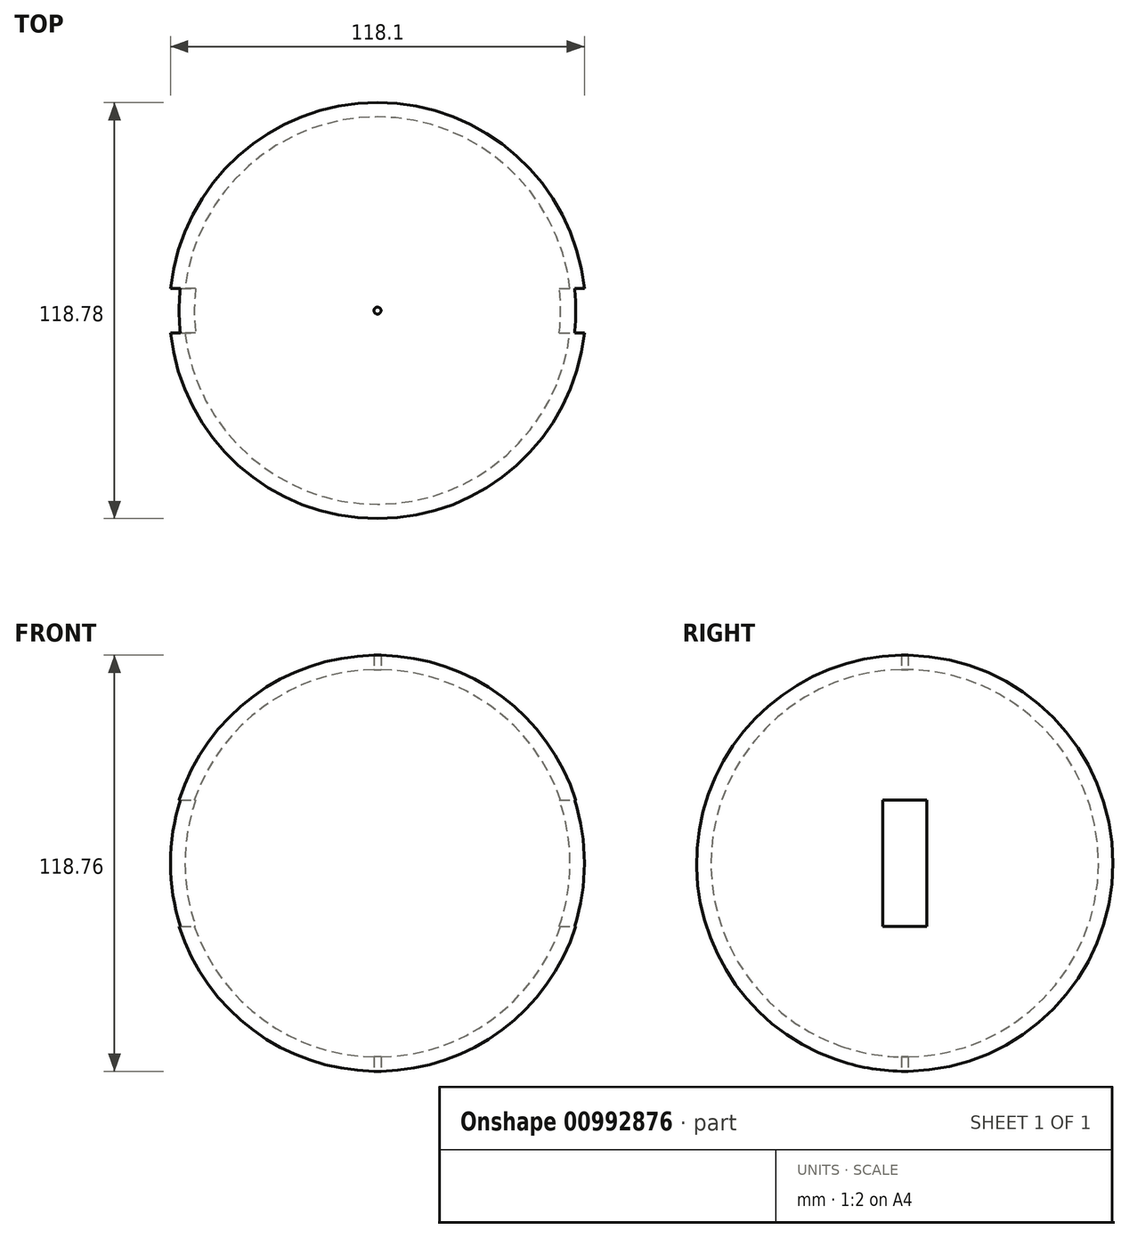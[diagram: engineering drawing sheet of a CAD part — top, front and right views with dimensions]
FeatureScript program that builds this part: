
annotation { "Feature Type Name" : "Feature", "Feature Type Description" : "" }
export const myFeature = defineFeature(function(context is Context, id is Id, definition is map)
    precondition{}
    {
        {
            var Q0;
            Q0=qCreatedBy(makeId("Top.planeOp"),FACE);
            var sketch = newSketch(context, id + "F0", { "sketchPlane" : qUnion([Q0])});
            skArc(sketch, "E0", {"start": v(55.3, 0) * mm, "mid": v(0, 55.3) * mm, "end": v(-55.3, 0) * mm});
            skArc(sketch, "E1", {"start": v(59.4, 0) * mm, "mid": v(0, 59.4) * mm, "end": v(-59.4, 0) * mm});
            skLineSegment(sketch, "E2", {"start": v(-59.4, 0) * mm, "end": v(-55.3, 0) * mm});
            skLineSegment(sketch, "E3.trimOffspring", {"start": v(55.3, 0) * mm, "end": v(59.4, 0) * mm});
            skSolve(sketch);
        }
        {
            var Q0;
            Q0=qCreatedBy(makeId("Top.planeOp"),FACE);
            var sketch = newSketch(context, id + "F1", { "sketchPlane" : qUnion([Q0])});
            skLineSegment(sketch, "E4", {"start": v(0, 0) * mm, "end": v(69.02, 0) * mm});
            skSolve(sketch);
        }
        {
            var Q0;
            Q0=makeQuery(id+"F0.imprint","IMPRINT",FACE,{"disambiguationData":[TD([[makeQuery(id+"F0.imprint","IMPRINT",EDGE,{"derivedFrom":sQuery(id+"F0.wireOp",EDGE,"E0")}),-1.0]])]});
            var Q1;
            Q1=sQuery(id+"F1.wireOp",EDGE,"E4");
            revolve(context, id + "F2", {"surfaceOperationType" : NewSurfaceOperationType.NEW, "entities" : qUnion([Q0]), "axis" : qUnion([Q1]), "revolveType" : RevolveType.FULL});
        }
        {
            var Q0;
            Q0=qCreatedBy(makeId("Top.planeOp"),FACE);
            var sketch = newSketch(context, id + "F3", { "sketchPlane" : qUnion([Q0])});
            skCircle(sketch, "E5", {"center": v(0, 0) * mm, "radius": 1 * mm});
            skSolve(sketch);
        }
        {
            var Q0;
            Q0=makeQuery(id+"F3.imprint","IMPRINT",FACE,{"disambiguationData":[TD([[makeQuery(id+"F3.imprint","IMPRINT",EDGE,{"derivedFrom":sQuery(id+"F3.wireOp",EDGE,"E5")}),1.0]])]});
            extrude(context, id + "F4", {"entities" : qUnion([Q0]), "endBound" : BoundingType.SYMMETRIC, "depth" : 200 * mm, "offsetDistance" : 25 * mm});
        }
        {
            var Q0;
            Q0=makeQuery(id+"F4.opExtrude","SWEPT_BODY",BODY,{"disambiguationData":[OSD([sQuery(id+"F3.wireOp",EDGE,"E5")])]});
            var Q1;
            Q1=makeQuery(id+"F2.opRevolve","SWEPT_BODY",BODY,{"disambiguationData":[OSD([sQuery(id+"F0.wireOp",EDGE,"E0"),sQuery(id+"F0.wireOp",EDGE,"E1"),sQuery(id+"F0.wireOp",EDGE,"E2"),sQuery(id+"F0.wireOp",EDGE,"E3.trimOffspring")])]});
            booleanBodies(context, id + "F5", {"operationType" : BooleanOperationType.SUBTRACTION, "tools" : qUnion([Q0]), "targets" : qUnion([Q1])});
        }
        {
            var Q0;
            Q0=qCreatedBy(makeId("Right.planeOp"),FACE);
            var Q1;
            Q1=sQuery(id+"F0.wireOp",VERTEX,"E3.trimOffspring.end");
            cPlane(context, id + "F6", {"entities" : qUnion([Q0, Q1]), "cplaneType" : CPlaneType.PLANE_POINT, "offset" : 25 * mm, "width" : 150 * mm, "height" : 150 * mm});
        }
        {
            var Q0;
            Q0=qCreatedBy(id+"F6.planeOp",FACE);
            var sketch = newSketch(context, id + "F7", { "sketchPlane" : qUnion([Q0])});
            skLineSegment(sketch, "E6.bottom", {"start": v(6.33, 18.06) * mm, "end": v(-6.33, 18.06) * mm});
            skLineSegment(sketch, "E6.top", {"start": v(6.33, -18.06) * mm, "end": v(-6.33, -18.06) * mm});
            skLineSegment(sketch, "E6.left", {"start": v(6.33, 18.06) * mm, "end": v(6.33, -18.06) * mm});
            skLineSegment(sketch, "E6.right", {"start": v(-6.33, 18.06) * mm, "end": v(-6.33, -18.06) * mm});
            skPoint(sketch, "E6.middle", {"position": v(0, 0) * mm});
            skSolve(sketch);
        }
        {
            var Q0;
            Q0 = qSketchRegion(id + "F7", true);
            extrude(context, id + "F8", {"entities" : qUnion([Q0]), "operationType" : NewBodyOperationType.REMOVE, "endBound" : BoundingType.THROUGH_ALL, "oppositeDirection" : true, "depth" : 25 * mm, "offsetDistance" : 25 * mm});
        }
    });
